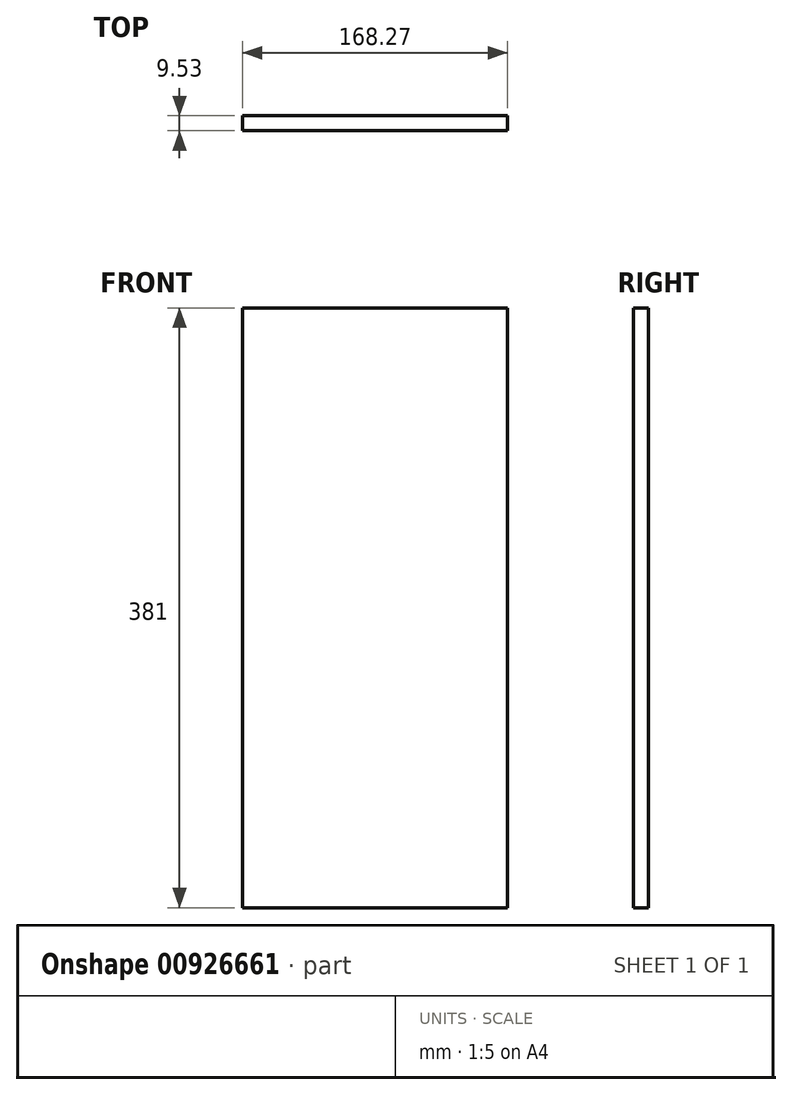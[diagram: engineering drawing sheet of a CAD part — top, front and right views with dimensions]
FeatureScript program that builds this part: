
annotation { "Feature Type Name" : "Feature", "Feature Type Description" : "" }
export const myFeature = defineFeature(function(context is Context, id is Id, definition is map)
    precondition{}
    {
        {
            var Q0;
            Q0=qCreatedBy(makeId("Front.planeOp"),FACE);
            var sketch = newSketch(context, id + "F0", { "sketchPlane" : qUnion([Q0])});
            skLineSegment(sketch, "E0.bottom", {"start": v(-48.53, 348.37) * mm, "end": v(119.74, 348.37) * mm});
            skLineSegment(sketch, "E0.top", {"start": v(-48.53, -32.63) * mm, "end": v(119.74, -32.63) * mm});
            skLineSegment(sketch, "E0.left", {"start": v(-48.53, 348.37) * mm, "end": v(-48.53, -32.63) * mm});
            skLineSegment(sketch, "E0.right", {"start": v(119.74, 348.37) * mm, "end": v(119.74, -32.63) * mm});
            skSolve(sketch);
        }
        {
            var Q0;
            Q0 = qSketchRegion(id + "F0", true);
            extrude(context, id + "F1", {"entities" : qUnion([Q0]), "depth" : 9.52 * mm, "offsetDistance" : 25.4 * mm});
        }
    });
